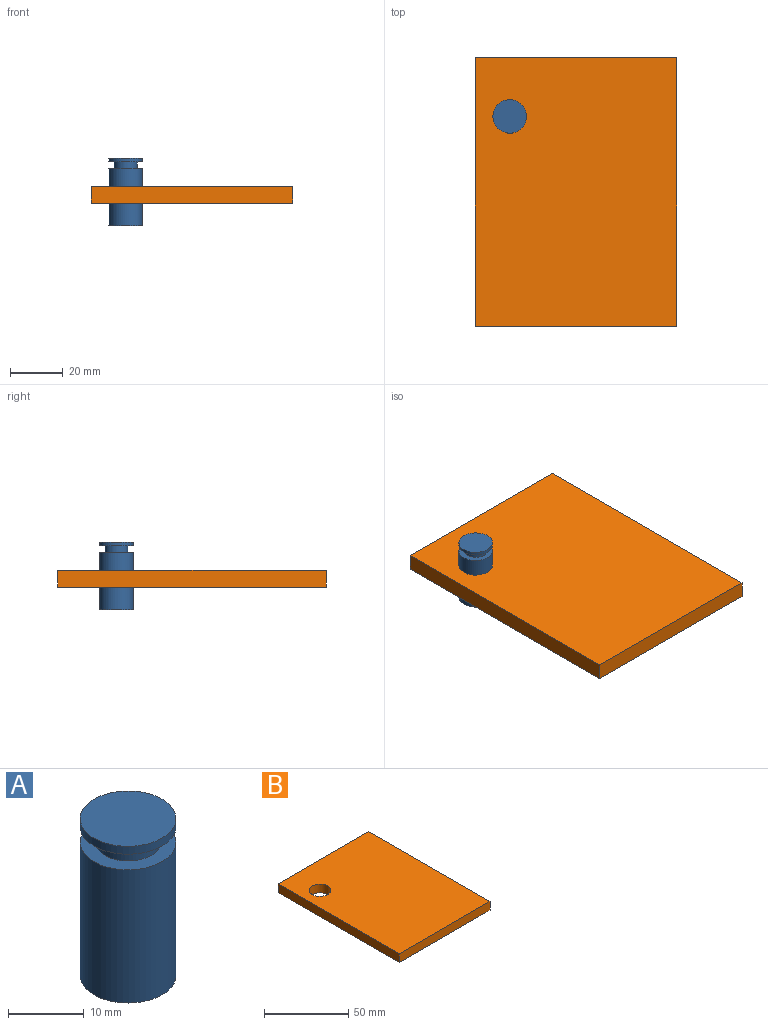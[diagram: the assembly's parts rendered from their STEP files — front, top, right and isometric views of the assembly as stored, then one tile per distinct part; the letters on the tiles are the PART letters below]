
ASSEMBLY  parts=2 mates=1
PART A: 7 faces, bbox 12.7x12.7x25.4 mm
  f0: cylinder r=6.35mm len=12.7mm, axis (0,0,-1), area 50.7mm2, adj f1,f2
  f1: plane 12.7x12.7mm, normal (0,0,1), area 126.7mm2, adj f0
  f2: plane 12.7x12.7mm, normal (0,0,-1), area 68.1mm2, adj f0,f3
  f3: cylinder r=4.32mm len=8.64mm, axis (0,0,1), area 68.9mm2, adj f2,f4
  f4: plane 12.7x12.7mm, normal (0,0,1), area 68.1mm2, adj f3,f6
  f5: plane 12.7x12.7mm, normal (0,0,-1), area 126.7mm2, adj f6
  f6: cylinder r=6.35mm len=21.59mm, axis (0,0,-1), area 861.4mm2, adj f4,f5
PART B: 7 faces, bbox 76.2x101.6x6.4 mm
  f0: plane 76.2x6.35mm, normal (0,1,0), area 483.9mm2, adj f1,f4,f5,f6
  f1: plane 101.6x6.35mm, normal (-1,0,0), area 645.2mm2, adj f0,f2,f5,f6
  f2: plane 76.2x6.35mm, normal (0,-1,0), area 483.9mm2, adj f1,f4,f5,f6
  f3: cylinder r=6.35mm len=12.7mm, axis (0,0,-1), area 253.4mm2, adj f5,f6
  f4: plane 101.6x6.35mm, normal (1,0,0), area 645.2mm2, adj f0,f2,f5,f6
  f5: plane 101.6x76.2mm, normal (0,0,1), area 7615.2mm2, adj f0,f1,f2,f3,f4
  f6: plane 101.6x76.2mm, normal (0,0,-1), area 7615.2mm2, adj f0,f1,f2,f3,f4
PLACE A t=(-31.93,6.51,17.68)mm
PLACE B t=(-6.81,-22.09,13.46)mm
MATE slider B.f3 <-> A.f0  axis (0,0,-1) through (-31.93,6.51,16.64)mm
